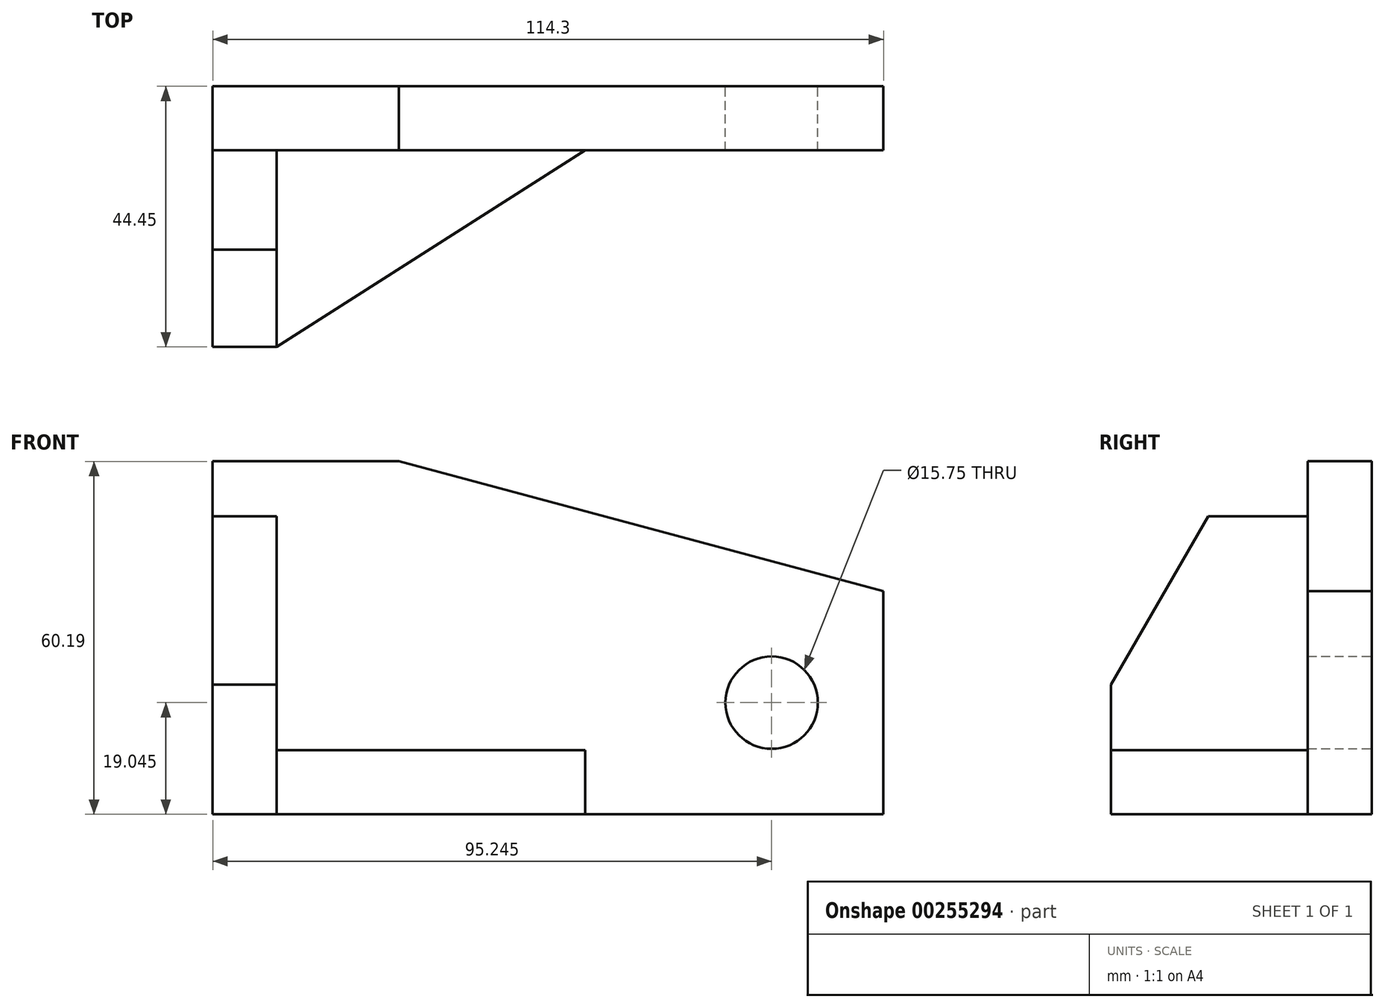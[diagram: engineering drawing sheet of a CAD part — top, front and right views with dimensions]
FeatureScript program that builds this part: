
annotation { "Feature Type Name" : "Feature", "Feature Type Description" : "" }
export const myFeature = defineFeature(function(context is Context, id is Id, definition is map)
    precondition{}
    {
        {
            var Q0;
            Q0=qCreatedBy(makeId("Front.planeOp"),FACE);
            var sketch = newSketch(context, id + "F0", { "sketchPlane" : qUnion([Q0])});
            skLineSegment(sketch, "E0.top", {"start": v(-63.35, -38.82) * mm, "end": v(50.95, -38.82) * mm});
            skLineSegment(sketch, "E0.left", {"start": v(-63.35, 21.37) * mm, "end": v(-63.35, -38.82) * mm});
            skLineSegment(sketch, "E1", {"start": v(-31.6, 21.37) * mm, "end": v(50.95, -0.75) * mm});
            skCircle(sketch, "E2", {"center": v(31.9, -19.77) * mm, "radius": 7.87 * mm});
            skLineSegment(sketch, "E3", {"start": v(50.95, -0.75) * mm, "end": v(50.95, -38.82) * mm});
            skLineSegment(sketch, "E4", {"start": v(-63.35, 21.37) * mm, "end": v(-31.6, 21.37) * mm});
            skSolve(sketch);
        }
        {
            var Q0;
            {var subQ1=sQuery(id+"F0.wireOp",EDGE,"E0.top");Q0=makeQuery(id+"F0.imprint","IMPRINT",FACE,{"disambiguationData":[TD([[makeQuery(id+"F0.imprint","IMPRINT",EDGE,{"derivedFrom":subQ1}),1.0]])]});}
            extrude(context, id + "F1", {"entities" : qUnion([Q0]), "depth" : 10.92 * mm});
        }
        {
            var Q0;
            Q0=makeQuery(id+"F1.opExtrude","SWEPT_FACE",FACE,{"disambiguationData":[OSD([sQuery(id+"F0.wireOp",EDGE,"E0.left")])]});
            var sketch = newSketch(context, id + "F2", { "sketchPlane" : qUnion([Q0])});
            skLineSegment(sketch, "E5.bottom", {"start": v(10.92, -38.82) * mm, "end": v(44.45, -38.82) * mm});
            skLineSegment(sketch, "E5.top", {"start": v(10.92, 11.98) * mm, "end": v(44.45, 11.98) * mm});
            skLineSegment(sketch, "E5.left", {"start": v(10.92, -38.82) * mm, "end": v(10.92, 11.98) * mm});
            skLineSegment(sketch, "E5.right", {"start": v(44.45, -38.82) * mm, "end": v(44.45, 11.98) * mm});
            skLineSegment(sketch, "E6", {"start": v(27.88, 11.98) * mm, "end": v(44.45, -16.73) * mm});
            skSolve(sketch);
        }
        {
            var Q0;
            {var subQ1=sQuery(id+"F2.wireOp",EDGE,"E5.bottom");Q0=makeQuery(id+"F2.imprint","IMPRINT",FACE,{"disambiguationData":[TD([[makeQuery(id+"F2.imprint","IMPRINT",EDGE,{"derivedFrom":subQ1}),1.0]])]});}
            extrude(context, id + "F3", {"entities" : qUnion([Q0]), "operationType" : NewBodyOperationType.ADD, "oppositeDirection" : true, "depth" : 10.92 * mm});
        }
        {
            var Q0;
            Q0=makeQuery(id+"F3.boolean.opBoolean","MERGE",FACE,{"derivedFrom":[makeQuery(id+"F1.opExtrude","SWEPT_FACE",FACE,{"disambiguationData":[OSD([sQuery(id+"F0.wireOp",EDGE,"E0.top")])]}),makeQuery(id+"F3.opExtrude","SWEPT_FACE",FACE,{"disambiguationData":[OSD([sQuery(id+"F2.wireOp",EDGE,"E5.bottom")])]})]});
            var sketch = newSketch(context, id + "F4", { "sketchPlane" : qUnion([Q0])});
            skLineSegment(sketch, "E7", {"start": v(-52.43, 44.45) * mm, "end": v(0.15, 10.92) * mm});
            skSolve(sketch);
        }
        {
            var Q0;
            Q0 = qSketchRegion(id + "F4", true);
            var Q1;
            {var subQ0=sQuery(id+"F4.wireOp",EDGE,"E7");Q1=makeQuery(id+"F4.imprint","IMPRINT",FACE,{"disambiguationData":[TD([[makeQuery(id+"F4.imprint","IMPRINT",EDGE,{"derivedFrom":subQ0}),-1.0]])]});}
            extrude(context, id + "F5", {"entities" : qUnion([Q0, Q1]), "operationType" : NewBodyOperationType.ADD, "oppositeDirection" : true, "depth" : 10.92 * mm});
        }
    });
